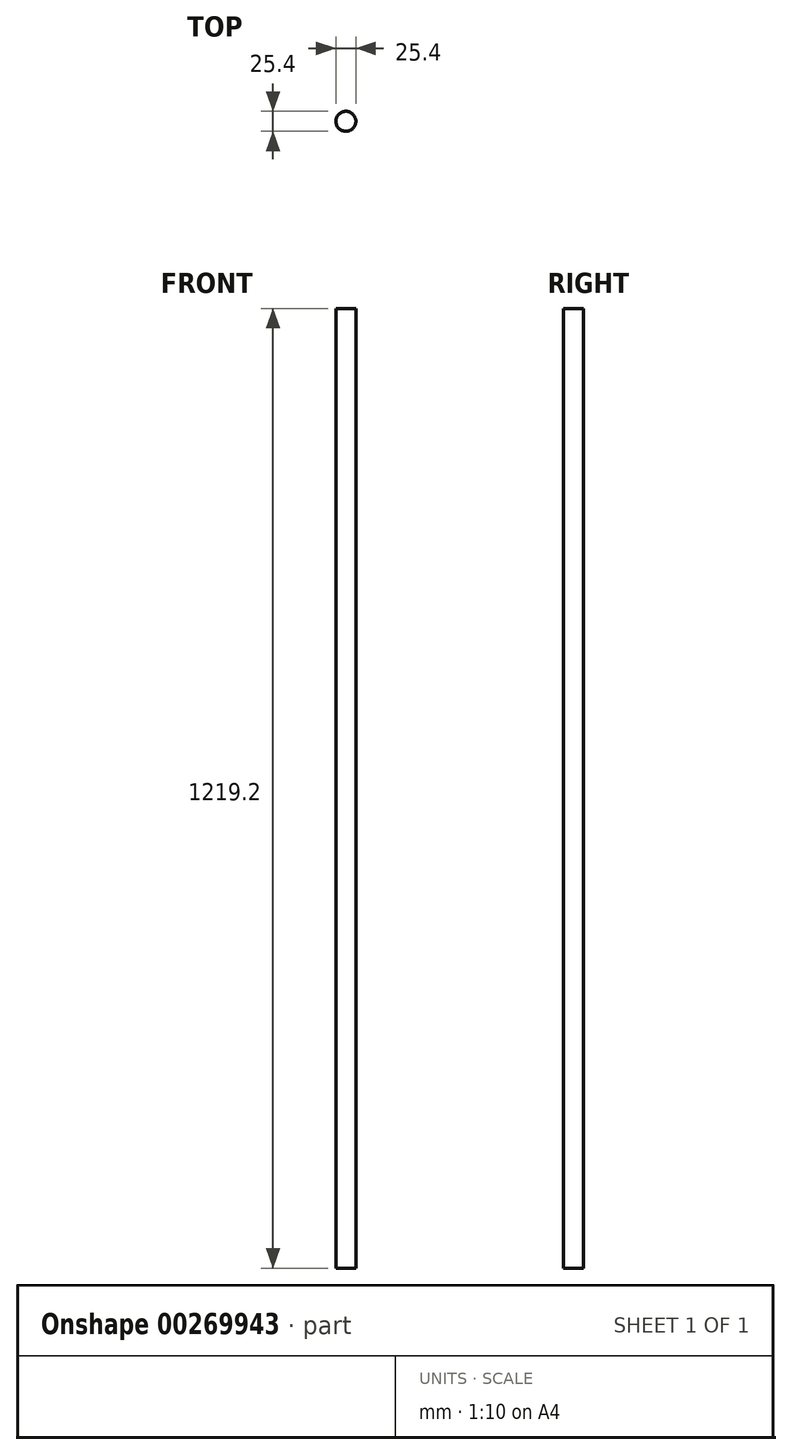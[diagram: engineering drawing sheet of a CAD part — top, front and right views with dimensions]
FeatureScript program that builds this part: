
annotation { "Feature Type Name" : "Feature", "Feature Type Description" : "" }
export const myFeature = defineFeature(function(context is Context, id is Id, definition is map)
    precondition{}
    {
        {
            var Q0;
            Q0=qCreatedBy(makeId("Top.planeOp"),FACE);
            var sketch = newSketch(context, id + "F0", { "sketchPlane" : qUnion([Q0])});
            skCircle(sketch, "E0", {"center": v(0, 0) * mm, "radius": 12.7 * mm});
            skSolve(sketch);
        }
        {
            var Q0;
            Q0 = qSketchRegion(id + "F0", true);
            extrude(context, id + "F1", {"entities" : qUnion([Q0]), "depth" : 1219.2 * mm});
        }
    });
